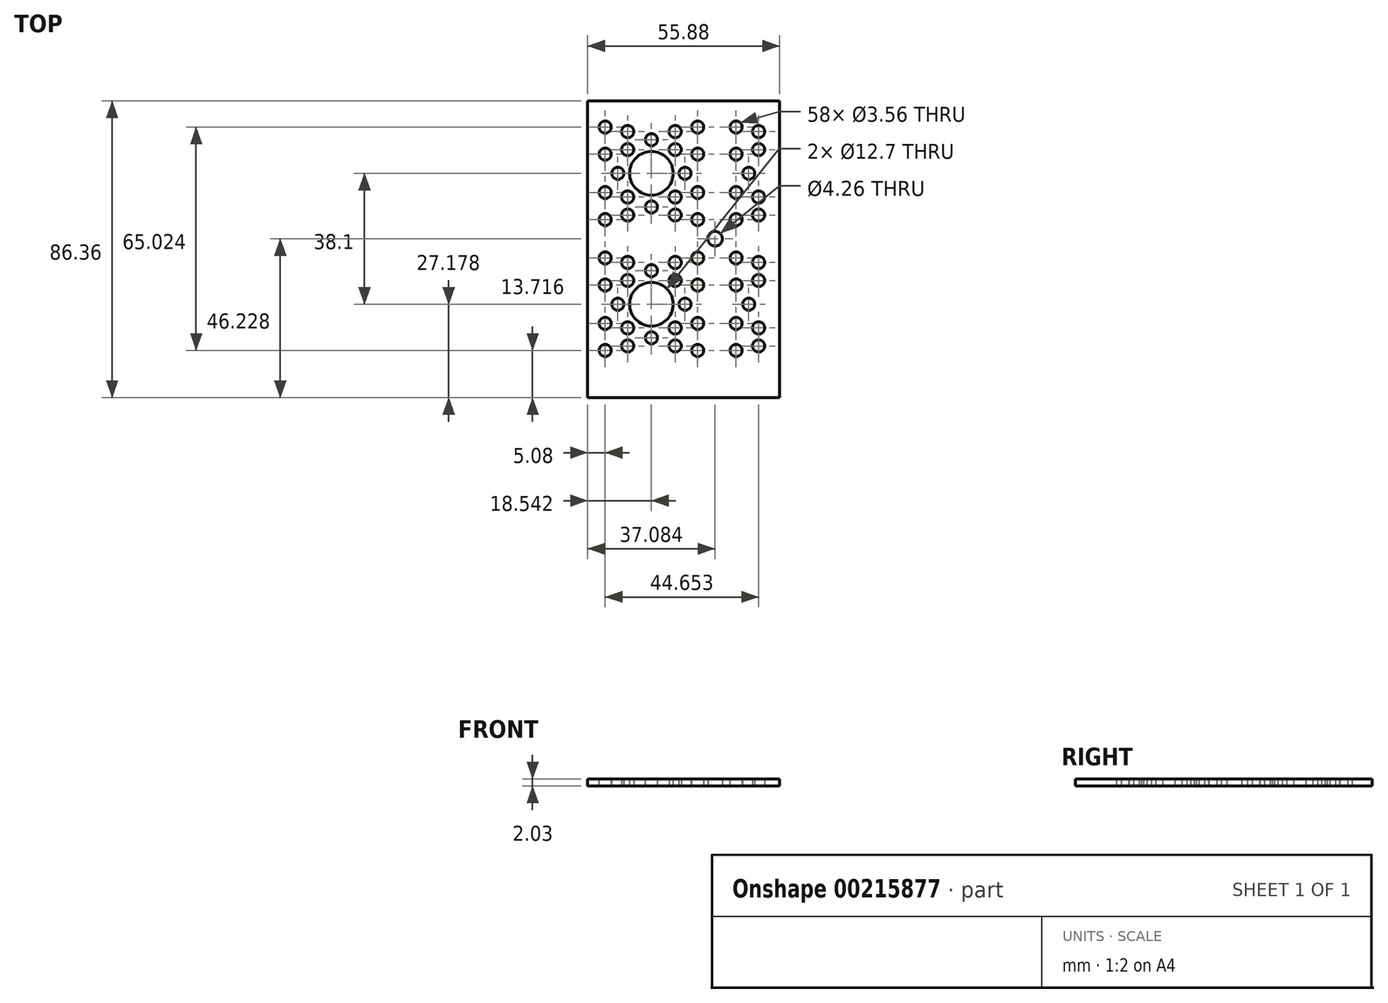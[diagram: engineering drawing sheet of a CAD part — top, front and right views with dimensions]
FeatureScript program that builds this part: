
annotation { "Feature Type Name" : "Feature", "Feature Type Description" : "" }
export const myFeature = defineFeature(function(context is Context, id is Id, definition is map)
    precondition{}
    {
        {
            var Q0;
            Q0=qCreatedBy(makeId("Top.planeOp"),FACE);
            var sketch = newSketch(context, id + "F0", { "sketchPlane" : qUnion([Q0])});
            skLineSegment(sketch, "E0.top", {"start": v(0, 86.36) * mm, "end": v(55.88, 86.36) * mm});
            skLineSegment(sketch, "E0.left", {"start": v(0, 0) * mm, "end": v(0, 86.36) * mm});
            skLineSegment(sketch, "E0.right", {"start": v(55.88, 0) * mm, "end": v(55.88, 86.36) * mm});
            skCircle(sketch, "E1", {"center": v(18.54, 65.28) * mm, "radius": 6.35 * mm});
            skCircle(sketch, "E2", {"center": v(18.54, 75.06) * mm, "radius": 1.78 * mm});
            skCircle(sketch, "E3", {"center": v(25.45, 77.42) * mm, "radius": 1.78 * mm});
            skCircle(sketch, "E4", {"center": v(25.45, 72.19) * mm, "radius": 1.78 * mm});
            skCircle(sketch, "E5", {"center": v(32, 78.74) * mm, "radius": 1.78 * mm});
            skCircle(sketch, "E6", {"center": v(32, 70.87) * mm, "radius": 1.78 * mm});
            skLineSegment(sketch, "E7", {"start": v(18.54, 65.28) * mm, "end": v(37.6, 65.28) * mm, "construction": true});
            skLineSegment(sketch, "E8", {"start": v(18.54, 65.28) * mm, "end": v(18.54, 56.81) * mm, "construction": true});
            skCircle(sketch, "E9.MirrorC", {"center": v(11.63, 77.42) * mm, "radius": 1.78 * mm});
            skCircle(sketch, "E10.MirrorC", {"center": v(5.08, 78.74) * mm, "radius": 1.78 * mm});
            skCircle(sketch, "E11.MirrorC", {"center": v(8.76, 65.28) * mm, "radius": 1.78 * mm});
            skCircle(sketch, "E12.MirrorC", {"center": v(11.63, 72.19) * mm, "radius": 1.78 * mm});
            skCircle(sketch, "E13.MirrorC", {"center": v(5.08, 70.87) * mm, "radius": 1.78 * mm});
            skCircle(sketch, "E14.MirrorC", {"center": v(5.08, 51.82) * mm, "radius": 1.78 * mm});
            skCircle(sketch, "E15.MirrorC", {"center": v(18.54, 55.5) * mm, "radius": 1.78 * mm});
            skCircle(sketch, "E16.MirrorC", {"center": v(11.63, 58.37) * mm, "radius": 1.78 * mm});
            skCircle(sketch, "E17.MirrorC", {"center": v(25.45, 53.14) * mm, "radius": 1.78 * mm});
            skCircle(sketch, "E18.MirrorC", {"center": v(11.63, 53.14) * mm, "radius": 1.78 * mm});
            skCircle(sketch, "E19.MirrorC", {"center": v(25.45, 58.37) * mm, "radius": 1.78 * mm});
            skCircle(sketch, "E20.MirrorC", {"center": v(32, 51.82) * mm, "radius": 1.78 * mm});
            skCircle(sketch, "E21.MirrorC", {"center": v(5.08, 59.7) * mm, "radius": 1.78 * mm});
            skCircle(sketch, "E22.MirrorC", {"center": v(32, 59.7) * mm, "radius": 1.78 * mm});
            skCircle(sketch, "E23.MirrorC", {"center": v(28.32, 65.28) * mm, "radius": 1.78 * mm});
            skLineSegment(sketch, "E24", {"start": v(18.54, 65.28) * mm, "end": v(18.54, 46.23) * mm, "construction": true});
            skLineSegment(sketch, "E25", {"start": v(18.54, 46.23) * mm, "end": v(28.28, 46.23) * mm, "construction": true});
            skCircle(sketch, "E26.MirrorC", {"center": v(8.76, 27.18) * mm, "radius": 1.78 * mm});
            skCircle(sketch, "E27.MirrorC", {"center": v(11.63, 15.04) * mm, "radius": 1.78 * mm});
            skCircle(sketch, "E28.MirrorC", {"center": v(5.08, 21.59) * mm, "radius": 1.78 * mm});
            skCircle(sketch, "E29.MirrorC", {"center": v(25.45, 34.09) * mm, "radius": 1.78 * mm});
            skCircle(sketch, "E30.MirrorC", {"center": v(5.08, 32.77) * mm, "radius": 1.78 * mm});
            skCircle(sketch, "E31.MirrorC", {"center": v(25.45, 39.32) * mm, "radius": 1.78 * mm});
            skCircle(sketch, "E32.MirrorC", {"center": v(32, 21.59) * mm, "radius": 1.78 * mm});
            skCircle(sketch, "E33.MirrorC", {"center": v(32, 13.72) * mm, "radius": 1.78 * mm});
            skCircle(sketch, "E34.MirrorC", {"center": v(25.45, 15.04) * mm, "radius": 1.78 * mm});
            skCircle(sketch, "E35.MirrorC", {"center": v(11.63, 20.27) * mm, "radius": 1.78 * mm});
            skCircle(sketch, "E36.MirrorC", {"center": v(32, 32.77) * mm, "radius": 1.78 * mm});
            skCircle(sketch, "E37.MirrorC", {"center": v(28.32, 27.18) * mm, "radius": 1.78 * mm});
            skCircle(sketch, "E38.MirrorC", {"center": v(18.54, 17.4) * mm, "radius": 1.78 * mm});
            skLineSegment(sketch, "E39.MirrorCS", {"start": v(18.54, 27.18) * mm, "end": v(18.54, 35.65) * mm, "construction": true});
            skCircle(sketch, "E40.MirrorC", {"center": v(18.54, 36.96) * mm, "radius": 1.78 * mm});
            skCircle(sketch, "E41.MirrorC", {"center": v(5.08, 13.72) * mm, "radius": 1.78 * mm});
            skCircle(sketch, "E42.MirrorC", {"center": v(11.63, 39.32) * mm, "radius": 1.78 * mm});
            skCircle(sketch, "E43.MirrorC", {"center": v(11.63, 34.09) * mm, "radius": 1.78 * mm});
            skCircle(sketch, "E44.MirrorC", {"center": v(18.54, 27.18) * mm, "radius": 6.35 * mm});
            skCircle(sketch, "E45.MirrorC", {"center": v(25.45, 20.27) * mm, "radius": 1.78 * mm});
            skCircle(sketch, "E46.MirrorC", {"center": v(32, 40.64) * mm, "radius": 1.78 * mm});
            skCircle(sketch, "E47.MirrorC", {"center": v(5.08, 40.64) * mm, "radius": 1.78 * mm});
            skCircle(sketch, "E48", {"center": v(18.54, 46.23) * mm, "radius": 1.78 * mm, "construction": true});
            skLineSegment(sketch, "E49", {"start": v(37.6, 65.28) * mm, "end": v(37.6, 57.98) * mm, "construction": true});
            skCircle(sketch, "E50.MirrorC", {"center": v(49.73, 53.14) * mm, "radius": 1.78 * mm});
            skCircle(sketch, "E51.MirrorC", {"center": v(49.73, 58.37) * mm, "radius": 1.78 * mm});
            skCircle(sketch, "E52.MirrorC", {"center": v(46.86, 65.28) * mm, "radius": 1.78 * mm});
            skCircle(sketch, "E53.MirrorC", {"center": v(49.73, 72.19) * mm, "radius": 1.78 * mm});
            skCircle(sketch, "E54.MirrorC", {"center": v(49.73, 77.42) * mm, "radius": 1.78 * mm});
            skCircle(sketch, "E55.MirrorC", {"center": v(43.18, 59.7) * mm, "radius": 1.78 * mm});
            skCircle(sketch, "E56.MirrorC", {"center": v(43.18, 70.87) * mm, "radius": 1.78 * mm});
            skCircle(sketch, "E57.MirrorC", {"center": v(43.18, 78.74) * mm, "radius": 1.78 * mm});
            skCircle(sketch, "E58.MirrorC", {"center": v(43.18, 51.82) * mm, "radius": 1.78 * mm});
            skCircle(sketch, "E59.MirrorC", {"center": v(46.86, 27.18) * mm, "radius": 1.78 * mm});
            skCircle(sketch, "E60.MirrorC", {"center": v(49.73, 34.09) * mm, "radius": 1.78 * mm});
            skCircle(sketch, "E61.MirrorC", {"center": v(49.73, 20.27) * mm, "radius": 1.78 * mm});
            skCircle(sketch, "E62.MirrorC", {"center": v(49.73, 15.04) * mm, "radius": 1.78 * mm});
            skCircle(sketch, "E63.MirrorC", {"center": v(49.73, 39.32) * mm, "radius": 1.78 * mm});
            skCircle(sketch, "E64.MirrorC", {"center": v(43.18, 21.59) * mm, "radius": 1.78 * mm});
            skCircle(sketch, "E65.MirrorC", {"center": v(43.18, 13.72) * mm, "radius": 1.78 * mm});
            skCircle(sketch, "E66.MirrorC", {"center": v(43.18, 32.77) * mm, "radius": 1.78 * mm});
            skCircle(sketch, "E67.MirrorC", {"center": v(43.18, 40.64) * mm, "radius": 1.78 * mm});
            skLineSegment(sketch, "E68", {"start": v(18.54, 27.18) * mm, "end": v(18.54, 8.13) * mm, "construction": true});
            skLineSegment(sketch, "E69", {"start": v(18.54, 8.13) * mm, "end": v(23.21, 8.13) * mm, "construction": true});
            skCircle(sketch, "E70", {"center": v(37.08, 46.23) * mm, "radius": 2.13 * mm});
            skLineSegment(sketch, "E71", {"start": v(0, 0) * mm, "end": v(55.88, 0) * mm});
            skSolve(sketch);
        }
        {
            var Q0;
            Q0 = qSketchRegion(id + "F0", true);
            extrude(context, id + "F1", {"entities" : qUnion([Q0]), "depth" : 2.03 * mm});
        }
    });
